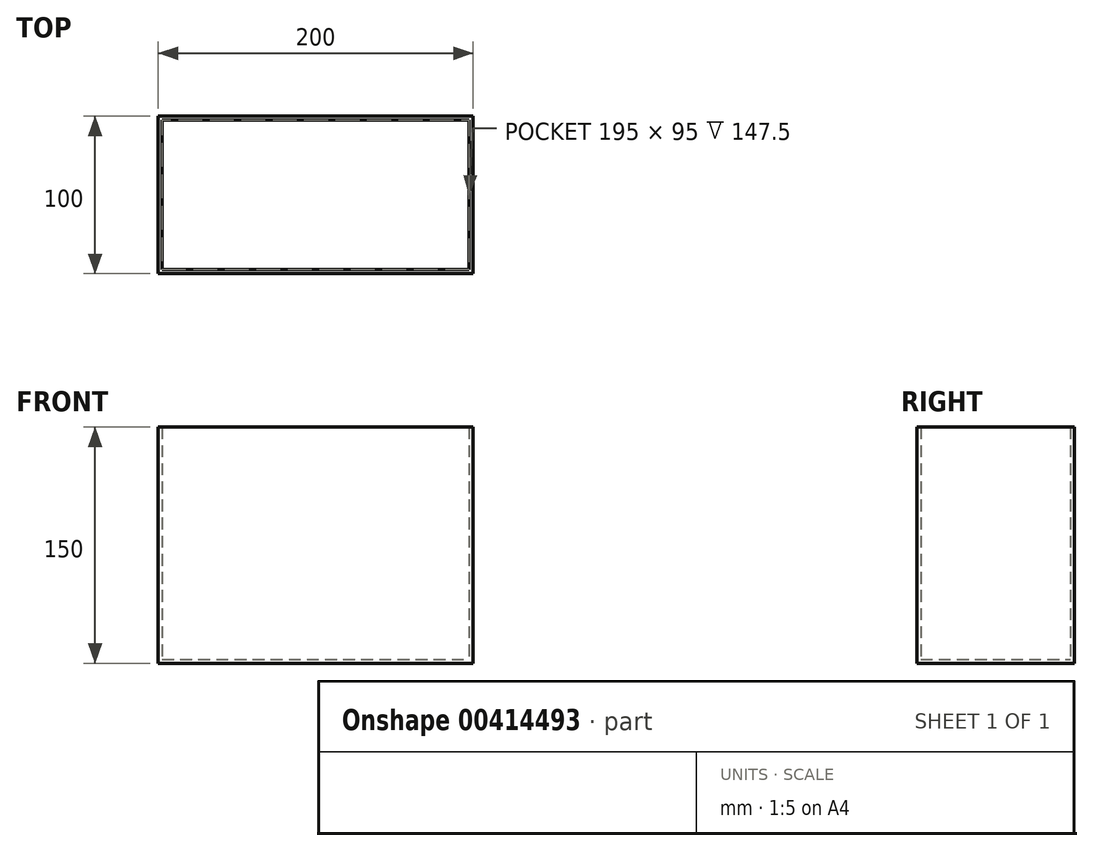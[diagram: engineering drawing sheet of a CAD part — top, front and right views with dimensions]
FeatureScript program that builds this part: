
annotation { "Feature Type Name" : "Feature", "Feature Type Description" : "" }
export const myFeature = defineFeature(function(context is Context, id is Id, definition is map)
    precondition{}
    {
        {
            var Q0;
            Q0=qCreatedBy(makeId("Top.planeOp"),FACE);
            var sketch = newSketch(context, id + "F0", { "sketchPlane" : qUnion([Q0])});
            skLineSegment(sketch, "E0.bottom", {"start": v(0, 0) * mm, "end": v(200, 0) * mm});
            skLineSegment(sketch, "E0.top", {"start": v(0, 100) * mm, "end": v(200, 100) * mm});
            skLineSegment(sketch, "E0.left", {"start": v(0, 0) * mm, "end": v(0, 100) * mm});
            skLineSegment(sketch, "E0.right", {"start": v(200, 0) * mm, "end": v(200, 100) * mm});
            skSolve(sketch);
        }
        {
            var Q0;
            Q0=makeQuery(id+"F0.imprint","IMPRINT",FACE,{"disambiguationData":[TD([[makeQuery(id+"F0.imprint","IMPRINT",EDGE,{"derivedFrom":sQuery(id+"F0.wireOp",EDGE,"E0.bottom")}),1.0]])]});
            extrude(context, id + "F1", {"entities" : qUnion([Q0]), "depth" : 150 * mm, "offsetDistance" : 25 * mm});
        }
        {
            var Q0;
            Q0=makeQuery(id+"F1.opExtrude","CAP_FACE",FACE,{"disambiguationData":[OSD([sQuery(id+"F0.wireOp",EDGE,"E0.bottom"),sQuery(id+"F0.wireOp",EDGE,"E0.top"),sQuery(id+"F0.wireOp",EDGE,"E0.left"),sQuery(id+"F0.wireOp",EDGE,"E0.right")])],"isStart":false});
            shell(context, id + "F2", {"entities" : qUnion([Q0]), "thickness" : 2.5 * mm});
        }
    });
